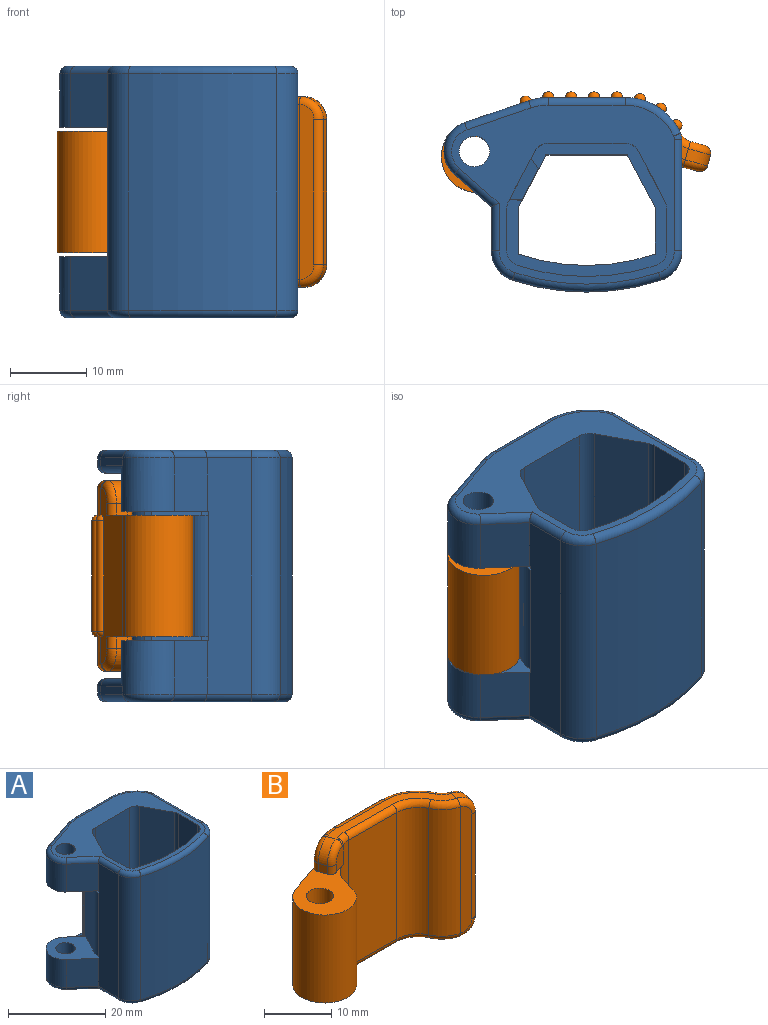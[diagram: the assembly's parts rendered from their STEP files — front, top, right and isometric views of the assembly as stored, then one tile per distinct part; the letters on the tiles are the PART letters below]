
ASSEMBLY  parts=2 mates=1
PART A: 107 faces, bbox 32x28.8x33 mm
  f0: plane 11.92x11.48mm, normal (0,0,1), area 71.6mm2, adj f7,f8,f9,f19,f23,f39,f40,f41
  f1: plane 21x17.5mm, normal (0,0,1), area 91.8mm2, adj f2,f3,f4,f5,f6,f20,f29,f30
  f2: plane 6.08x3mm, normal (1,0,0), area 18.2mm2, adj f1,f3,f20,f22
  f3: plane 6.93x3.65mm, normal (0.88,-0.47,0), area 23.5mm2, adj f1,f2,f4,f22
  f4: plane 10.69x3mm, normal (0,-1,0), area 32.1mm2, adj f1,f3,f5,f22
  f5: plane 6.93x3.65mm, normal (-0.88,-0.47,0), area 23.5mm2, adj f1,f4,f6,f22
  f6: plane 6.08x3mm, normal (-1,0,0), area 18.2mm2, adj f1,f5,f20,f22
  f7: cylinder r=4mm len=7.01mm, axis (0,0,-1), area 80.7mm2, adj f0,f8,f18,f21,f23,f76,f96
  f8: plane 7x4.87mm, normal (-0.66,-0.75,0), area 45.2mm2, adj f0,f7,f9,f78
  f9: plane 31x5.8mm, normal (-1,0,0), area 176.3mm2, adj f0,f8,f10,f43,f46,f52,f62,f77
  f10: cylinder r=4mm len=31mm, axis (0,0,-1), area 155.6mm2, adj f9,f11,f75,f87
  f11: cylinder r=31.35mm len=31mm, axis (0,0,-1), area 614.3mm2, adj f10,f12,f73,f85
  f12: cylinder r=4mm len=31mm, axis (0,0,-1), area 155.6mm2, adj f11,f13,f71,f83
  f13: plane 31x14.64mm, normal (1,0,0), area 191.5mm2, adj f12,f14,f24,f53,f69,f81,f91,f97
  f14: cylinder r=2mm len=1mm, axis (0,0,-1), area 0.9mm2, adj f13,f15,f67,f92
  f15: cylinder r=8mm len=7.28mm, axis (0,0,-1), area 9.1mm2, adj f14,f16,f68,f93
  f16: plane 10.09x1mm, normal (0,1,0), area 10.1mm2, adj f15,f17,f70,f94
  f17: cylinder r=8mm len=2.58mm, axis (0,0,-1), area 2.6mm2, adj f16,f18,f72,f95
  f18: plane 8.4x2.86mm, normal (-0.32,0.95,0), area 8.9mm2, adj f7,f17,f74,f96
  f19: cylinder r=2mm len=8mm, axis (0,0,-1), area 100.5mm2, adj f0,f22
  f20: cylinder r=27.85mm len=18mm, axis (0,0,-1), area 55mm2, adj f1,f2,f6,f22
  f21: plane 24.7x10.67mm, normal (0,0,1), area 81.7mm2, adj f7,f23,f25,f26,f27,f28,f41,f91
  f22: plane 29.23x23.5mm, normal (0,0,-1), area 314.2mm2, adj f2,f3,f4,f5,f6,f19,f20,f67
  f23: plane 5x3.15mm, normal (0.66,0.75,0), area 20.9mm2, adj f0,f7,f21,f41
  f24: cylinder r=4mm len=29mm, axis (0,0,-1), area 54.7mm2, adj f13,f25,f91,f97
  f25: plane 27.36x6.6mm, normal (0.88,0.47,0), area 200.1mm2, adj f21,f24,f26,f63,f91,f97
  f26: cylinder r=4mm len=27mm, axis (0,0,-1), area 117.2mm2, adj f21,f25,f27,f63
  f27: plane 27x10.09mm, normal (0,1,0), area 272.4mm2, adj f21,f26,f28,f63
  f28: cylinder r=4mm len=27mm, axis (0,0,-1), area 117.2mm2, adj f21,f27,f41,f42,f63,f66
  f29: cylinder r=2mm len=30mm, axis (0,0,-1), area 65.1mm2, adj f1,f30,f40,f42,f60,f64
  f30: plane 30x10.09mm, normal (0,-1,0), area 302.6mm2, adj f1,f29,f31,f64
  f31: cylinder r=2mm len=30mm, axis (0,0,-1), area 65.1mm2, adj f1,f30,f32,f64
  f32: plane 30x6.55mm, normal (-0.88,-0.47,0), area 222.2mm2, adj f1,f31,f33,f64
  f33: cylinder r=2mm len=30mm, axis (0,0,-1), area 29.1mm2, adj f1,f32,f34,f64
  f34: plane 30x5.59mm, normal (-1,0,0), area 167.8mm2, adj f1,f33,f35,f64
  f35: cylinder r=2mm len=30mm, axis (0,0,-1), area 75.3mm2, adj f1,f34,f36,f64
  f36: cylinder r=29.35mm len=30mm, axis (0,0,-1), area 556.5mm2, adj f1,f35,f37,f64
  f37: cylinder r=2mm len=30mm, axis (0,0,-1), area 75.3mm2, adj f1,f36,f38,f64
  f38: plane 30x5.59mm, normal (1,0,0), area 167.8mm2, adj f1,f37,f39,f43,f59,f64
  f39: cylinder r=2mm len=5mm, axis (0,0,-1), area 4.9mm2, adj f0,f1,f38,f40
  f40: plane 6.55x5mm, normal (0.88,-0.47,0), area 37mm2, adj f0,f1,f29,f39
  f41: plane 5x0.69mm, normal (-0.88,0.47,0), area 3.9mm2, adj f0,f21,f23,f28
  f42: plane 17x1.77mm, normal (-0.47,-0.88,0), area 34mm2, adj f0,f28,f29,f52
  f43: plane 17x2mm, normal (0,1,0), area 18mm2, adj f0,f9,f38,f47,f50,f51,f52
  f44: plane 16x1.33mm, normal (0.47,0.88,0), area 24mm2, adj f45,f50,f51,f103
  f45: plane 16x5.85mm, normal (-0.88,0.47,0), area 105.7mm2, adj f44,f46,f50,f51
  f46: cylinder r=4mm len=16mm, axis (0,0,-1), area 31.1mm2, adj f9,f45,f50,f51
  f47: cylinder r=3mm len=16mm, axis (0,0,-1), area 23.3mm2, adj f43,f48,f50,f51
  f48: plane 16x0.44mm, normal (-0.47,-0.88,0), area 8mm2, adj f47,f50,f51,f106
  f49: plane 14x4.08mm, normal (0.88,-0.47,0), area 64.5mm2, adj f103,f104,f105,f106
  f50: plane 7.71x4.87mm, normal (0,0,1), area 11.6mm2, adj f43,f44,f45,f46,f47,f48,f104
  f51: plane 7.71x4.87mm, normal (0,0,-1), area 11.6mm2, adj f43,f44,f45,f46,f47,f48,f105
  f52: plane 11.92x11.48mm, normal (0,0,-1), area 71.6mm2, adj f9,f42,f43,f58,f59,f60,f61,f62
  f53: cylinder r=2mm len=1mm, axis (0,0,1), area 0.9mm2, adj f13,f54,f79,f98
  f54: cylinder r=8mm len=7.28mm, axis (0,0,1), area 9.1mm2, adj f53,f55,f80,f99
  f55: plane 10.09x1mm, normal (0,1,0), area 10.1mm2, adj f54,f56,f82,f100
  f56: cylinder r=8mm len=2.58mm, axis (0,0,1), area 2.6mm2, adj f55,f57,f84,f101
  f57: plane 8.4x2.86mm, normal (-0.32,0.95,0), area 8.9mm2, adj f56,f58,f86,f102
  f58: cylinder r=4mm len=7.01mm, axis (0,0,1), area 80.7mm2, adj f52,f57,f62,f63,f65,f88,f102
  f59: cylinder r=2mm len=8mm, axis (0,0,1), area 7.8mm2, adj f38,f52,f60,f64
  f60: plane 8x6.55mm, normal (0.88,-0.47,0), area 59.3mm2, adj f29,f52,f59,f64
  f61: cylinder r=2mm len=8mm, axis (0,0,1), area 100.5mm2, adj f52,f64
  f62: plane 7x4.87mm, normal (-0.66,-0.75,0), area 45.2mm2, adj f9,f52,f58,f90
  f63: plane 24.7x10.67mm, normal (0,0,-1), area 81.7mm2, adj f25,f26,f27,f28,f58,f65,f66,f97
  f64: plane 29.23x23.5mm, normal (0,0,1), area 222.4mm2, adj f29,f30,f31,f32,f33,f34,f35,f36
  f65: plane 5x3.15mm, normal (0.66,0.75,0), area 20.9mm2, adj f52,f58,f63,f66
  f66: plane 5x0.69mm, normal (-0.88,0.47,0), area 3.9mm2, adj f28,f52,f63,f65
  f67: torus R=1mm, axis (0,0,1), area 1.1mm2, adj f14,f22,f68,f69
  f68: torus R=7mm, axis (0,0,1), area 13.7mm2, adj f15,f22,f67,f70
  f69: cylinder r=1mm len=14.64mm, axis (0,1,0), area 23mm2, adj f13,f22,f67,f71
  f70: cylinder r=1mm len=10.09mm, axis (-1,0,0), area 15.8mm2, adj f16,f22,f68,f72
  f71: torus R=3mm, axis (0,0,1), area 7.2mm2, adj f12,f22,f69,f73
  f72: torus R=7mm, axis (0,0,1), area 3.9mm2, adj f17,f22,f70,f74
  f73: torus R=30.35mm, axis (0,0,1), area 30.8mm2, adj f11,f22,f71,f75
  f74: cylinder r=1mm len=8.72mm, axis (-0.95,-0.32,0), area 13.9mm2, adj f18,f22,f72,f76
  f75: torus R=3mm, axis (0,0,1), area 7.2mm2, adj f10,f22,f73,f77
  f76: torus R=3mm, axis (0,0,1), area 12mm2, adj f7,f22,f74,f78
  f77: cylinder r=1mm len=6.26mm, axis (0,-1,0), area 9.5mm2, adj f9,f22,f75,f78
  f78: cylinder r=1mm len=5.87mm, axis (0.75,-0.66,0), area 10.5mm2, adj f8,f22,f76,f77
  f79: torus R=1mm, axis (0,0,-1), area 1.1mm2, adj f53,f64,f80,f81
  f80: torus R=7mm, axis (0,0,-1), area 13.7mm2, adj f54,f64,f79,f82
  f81: cylinder r=1mm len=14.64mm, axis (0,-1,0), area 23mm2, adj f13,f64,f79,f83
  f82: cylinder r=1mm len=10.09mm, axis (-1,0,0), area 15.8mm2, adj f55,f64,f80,f84
  f83: torus R=3mm, axis (0,0,-1), area 7.2mm2, adj f12,f64,f81,f85
  f84: torus R=7mm, axis (0,0,-1), area 3.9mm2, adj f56,f64,f82,f86
  f85: torus R=30.35mm, axis (0,0,-1), area 30.8mm2, adj f11,f64,f83,f87
  f86: cylinder r=1mm len=8.72mm, axis (-0.95,-0.32,0), area 13.9mm2, adj f57,f64,f84,f88
  f87: torus R=3mm, axis (0,0,-1), area 7.2mm2, adj f10,f64,f85,f89
  f88: torus R=3mm, axis (0,0,-1), area 12mm2, adj f58,f64,f86,f90
  f89: cylinder r=1mm len=6.26mm, axis (0,1,0), area 9.5mm2, adj f9,f64,f87,f90
  f90: cylinder r=1mm len=5.87mm, axis (0.75,-0.66,0), area 10.5mm2, adj f62,f64,f88,f89
  f91: cylinder r=1mm len=9.05mm, axis (0,-1,0), area 11.9mm2, adj f13,f21,f24,f25,f92
  f92: torus R=1mm, axis (0,0,1), area 1.1mm2, adj f14,f21,f91,f93
  f93: torus R=7mm, axis (0,0,1), area 13.7mm2, adj f15,f21,f92,f94
  f94: cylinder r=1mm len=10.09mm, axis (1,0,0), area 15.8mm2, adj f16,f21,f93,f95
  f95: torus R=7mm, axis (0,0,1), area 3.9mm2, adj f17,f21,f94,f96
  f96: cylinder r=1mm len=8.72mm, axis (0.95,0.32,0), area 11.9mm2, adj f7,f18,f21,f95
  f97: cylinder r=1mm len=9.05mm, axis (0,1,0), area 11.9mm2, adj f13,f24,f25,f63,f98
  f98: torus R=1mm, axis (0,0,-1), area 1.1mm2, adj f53,f63,f97,f99
  f99: torus R=7mm, axis (0,0,-1), area 13.7mm2, adj f54,f63,f98,f100
  f100: cylinder r=1mm len=10.09mm, axis (1,0,0), area 15.8mm2, adj f55,f63,f99,f101
  f101: torus R=7mm, axis (0,0,-1), area 3.9mm2, adj f56,f63,f100,f102
  f102: cylinder r=1mm len=8.72mm, axis (0.95,0.32,0), area 11.9mm2, adj f57,f58,f63,f101
  f103: plane 16x1.82mm, normal (0.81,0.58,0), area 33.5mm2, adj f44,f49,f104,f105
  f104: plane 5.89x4.39mm, normal (0.4,-0.21,0.89), area 12.5mm2, adj f49,f50,f103,f106
  f105: plane 5.89x4.39mm, normal (0.4,-0.21,-0.89), area 12.5mm2, adj f49,f51,f103,f106
  f106: plane 16x2.24mm, normal (-0.02,-1,0), area 33.5mm2, adj f48,f49,f104,f105
PART B: 87 faces, bbox 35.6x13.3x25.6 mm
  f0: cylinder r=2mm len=23mm, axis (0,0,-1), area 40.1mm2, adj f1,f13,f60,f64
  f1: cylinder r=8mm len=23mm, axis (0,0,-1), area 141.4mm2, adj f0,f2,f22,f23,f24,f59,f65,f71
  f2: plane 23x10.09mm, normal (0,1,0), area 149.7mm2, adj f1,f3,f25,f26,f27,f28,f58,f66
  f3: cylinder r=8mm len=23mm, axis (0,0,-1), area 43.5mm2, adj f2,f4,f17,f28,f57,f67,f77,f78
  f4: plane 23.07x8.46mm, normal (-0.32,0.95,0), area 138.9mm2, adj f3,f15,f16,f17,f18,f54,f55,f56
  f5: plane 1.5x1.42mm, normal (-0.95,-0.32,0), area 2.3mm2, adj f15,f36,f53,f70
  f6: plane 3.5x2.25mm, normal (0.32,-0.95,0), area 7.4mm2, adj f7,f15,f51,f52,f53
  f7: cylinder r=4.5mm len=23mm, axis (0,0,-1), area 104.7mm2, adj f6,f8,f15,f16,f21,f31,f40,f50
  f8: plane 23x10.09mm, normal (0,-1,0), area 232mm2, adj f7,f9,f41,f49
  f9: cylinder r=4.5mm len=23mm, axis (0,0,-1), area 118.2mm2, adj f8,f10,f42,f48
  f10: cylinder r=5.5mm len=23mm, axis (0,0,-1), area 110.4mm2, adj f9,f11,f43,f47
  f11: plane 23x1.93mm, normal (-0.27,-0.96,0), area 44.3mm2, adj f10,f44,f45,f46
  f12: plane 19x1.45mm, normal (0.96,-0.27,0), area 28.5mm2, adj f33,f35,f45,f62
  f13: plane 23x1.93mm, normal (0.27,0.96,0), area 44.3mm2, adj f0,f61,f62,f63
  f14: plane 21x7.18mm, normal (0,0,-1), area 34.4mm2, adj f35,f36,f47,f48,f49,f50,f51,f64
  f15: plane 12.59x11.27mm, normal (0,0,-1), area 67.8mm2, adj f4,f5,f6,f7,f18,f19,f20,f21
  f16: plane 12.59x11.27mm, normal (0,0,1), area 67.8mm2, adj f4,f7,f18,f19,f20,f21,f29,f30
  f17: cylinder r=0.75mm len=14.5mm, axis (0,0,-1), area 34.3mm2, adj f3,f4,f78,f86
  f18: cylinder r=4mm len=16mm, axis (0,0,-1), area 14.9mm2, adj f4,f15,f16,f19
  f19: cylinder r=4.75mm len=16mm, axis (0,0,-1), area 238.8mm2, adj f15,f16,f18,f20
  f20: cylinder r=4mm len=16mm, axis (0,0,-1), area 47.9mm2, adj f15,f16,f19,f21
  f21: plane 16x2.54mm, normal (0.97,-0.26,0), area 42mm2, adj f7,f15,f16,f20
  f22: cylinder r=0.75mm len=14.5mm, axis (0,0,-1), area 35.2mm2, adj f1,f73,f81
  f23: cylinder r=0.75mm len=14.5mm, axis (0,0,-1), area 35.2mm2, adj f1,f72,f80
  f24: cylinder r=0.75mm len=14.5mm, axis (0,0,-1), area 35.2mm2, adj f1,f71,f79
  f25: cylinder r=0.75mm len=14.5mm, axis (0,0,-1), area 34.2mm2, adj f2,f74,f82
  f26: cylinder r=0.75mm len=14.5mm, axis (0,0,-1), area 34.2mm2, adj f2,f75,f83
  f27: cylinder r=0.75mm len=14.5mm, axis (0,0,-1), area 34.2mm2, adj f2,f76,f84
  f28: cylinder r=0.75mm len=14.5mm, axis (0,0,-1), area 34.7mm2, adj f2,f3,f77,f85
  f29: cylinder r=2mm len=16mm, axis (0,0,-1), area 201.1mm2, adj f15,f16
  f30: plane 1.5x1.42mm, normal (-0.95,-0.32,0), area 2.3mm2, adj f16,f34,f37,f54
  f31: plane 3.5x2.25mm, normal (0.32,-0.95,0), area 7.4mm2, adj f7,f16,f37,f38,f39
  f32: plane 21x7.18mm, normal (0,0,1), area 34.4mm2, adj f33,f34,f39,f40,f41,f42,f43,f56
  f33: cylinder r=3mm len=3.29mm, axis (-0.27,-0.96,0), area 7.1mm2, adj f12,f32,f44,f61
  f34: cylinder r=3mm len=3.32mm, axis (-0.32,0.95,0), area 7.1mm2, adj f30,f32,f38,f55
  f35: cylinder r=3mm len=3.29mm, axis (0.27,0.96,0), area 7.1mm2, adj f12,f14,f46,f63
  f36: cylinder r=3mm len=3.32mm, axis (0.32,-0.95,0), area 7.1mm2, adj f5,f14,f52,f69
  f37: cylinder r=1mm len=1.5mm, axis (0,0,-1), area 2.4mm2, adj f16,f30,f31,f38
  f38: torus R=2mm, axis (-0.32,0.95,0), area 6.5mm2, adj f31,f34,f37,f39
  f39: cylinder r=1mm len=1.07mm, axis (-0.95,-0.32,0), area 0.6mm2, adj f31,f32,f38,f40
  f40: torus R=5.5mm, axis (0,0,1), area 2.5mm2, adj f7,f32,f39,f41
  f41: cylinder r=1mm len=10.09mm, axis (-1,0,0), area 15.8mm2, adj f8,f32,f40,f42
  f42: torus R=5.5mm, axis (0,0,1), area 8.7mm2, adj f9,f32,f41,f43
  f43: torus R=4.5mm, axis (0,0,1), area 7mm2, adj f10,f32,f42,f44
  f44: torus R=2mm, axis (0.27,0.96,0), area 6.5mm2, adj f11,f33,f43,f45
  f45: cylinder r=1mm len=19mm, axis (0,0,-1), area 29.8mm2, adj f11,f12,f44,f46
  f46: torus R=2mm, axis (0.27,0.96,0), area 6.5mm2, adj f11,f35,f45,f47
  f47: torus R=4.5mm, axis (0,0,1), area 7mm2, adj f10,f14,f46,f48
  f48: torus R=5.5mm, axis (0,0,1), area 8.7mm2, adj f9,f14,f47,f49
  f49: cylinder r=1mm len=10.09mm, axis (1,0,0), area 15.8mm2, adj f8,f14,f48,f50
  f50: torus R=5.5mm, axis (0,0,1), area 2.5mm2, adj f7,f14,f49,f51
  f51: cylinder r=1mm len=1.07mm, axis (0.95,0.32,0), area 0.6mm2, adj f6,f14,f50,f52
  f52: torus R=2mm, axis (-0.32,0.95,0), area 6.5mm2, adj f6,f36,f51,f53
  f53: cylinder r=1mm len=1.5mm, axis (0,0,-1), area 2.4mm2, adj f5,f6,f15,f52
  f54: cylinder r=1mm len=1.5mm, axis (0,0,-1), area 2.4mm2, adj f4,f16,f30,f55
  f55: torus R=2mm, axis (0.32,-0.95,0), area 6.5mm2, adj f4,f34,f54,f56
  f56: cylinder r=1mm len=1.07mm, axis (0.95,0.32,0), area 0.6mm2, adj f4,f32,f55,f57
  f57: torus R=7mm, axis (0,0,1), area 3.9mm2, adj f3,f32,f56,f58
  f58: cylinder r=1mm len=10.09mm, axis (1,0,0), area 15.8mm2, adj f2,f32,f57,f59
  f59: torus R=7mm, axis (0,0,1), area 13.7mm2, adj f1,f32,f58,f60
  f60: torus R=3mm, axis (0,0,1), area 3.2mm2, adj f0,f32,f59,f61
  f61: torus R=2mm, axis (0.27,0.96,0), area 6.5mm2, adj f13,f33,f60,f62
  f62: cylinder r=1mm len=19mm, axis (0,0,1), area 29.8mm2, adj f12,f13,f61,f63
  f63: torus R=2mm, axis (0.27,0.96,0), area 6.5mm2, adj f13,f35,f62,f64
  f64: torus R=3mm, axis (0,0,1), area 3.2mm2, adj f0,f14,f63,f65
  f65: torus R=7mm, axis (0,0,1), area 13.7mm2, adj f1,f14,f64,f66
  f66: cylinder r=1mm len=10.09mm, axis (-1,0,0), area 15.8mm2, adj f2,f14,f65,f67
  f67: torus R=7mm, axis (0,0,1), area 3.9mm2, adj f3,f14,f66,f68
  f68: cylinder r=1mm len=1.07mm, axis (-0.95,-0.32,0), area 0.6mm2, adj f4,f14,f67,f69
  f69: torus R=2mm, axis (0.32,-0.95,0), area 6.5mm2, adj f4,f36,f68,f70
  f70: cylinder r=1mm len=1.5mm, axis (0,0,-1), area 2.4mm2, adj f4,f5,f15,f69
  f71: sphere r=0.75mm, area 1.8mm2, adj f1,f24
  f72: sphere r=0.75mm, area 1.7mm2, adj f1,f23
  f73: sphere r=0.75mm, area 1.6mm2, adj f1,f22
  f74: sphere r=0.75mm, area 1.8mm2, adj f2,f25
  f75: sphere r=0.75mm, area 1.8mm2, adj f2,f26
  f76: sphere r=0.75mm, area 1.8mm2, adj f2,f27
  f77: sphere r=0.75mm, area 1.8mm2, adj f2,f3,f28
  f78: sphere r=0.75mm, area 1.8mm2, adj f3,f4,f17
  f79: sphere r=0.75mm, area 1.8mm2, adj f1,f24
  f80: sphere r=0.75mm, area 1.8mm2, adj f1,f23
  f81: sphere r=0.75mm, area 1.8mm2, adj f1,f22
  f82: sphere r=0.75mm, area 1.8mm2, adj f2,f25
  f83: sphere r=0.75mm, area 1.8mm2, adj f2,f26
  f84: sphere r=0.75mm, area 1.8mm2, adj f2,f27
  f85: sphere r=0.75mm, area 1.8mm2, adj f2,f3,f28
  f86: sphere r=0.75mm, area 1.8mm2, adj f3,f4,f17
PLACE A t=(-39.85,27.79,-19.96)mm fixed
PLACE B rot(axis=(0,0,-1),0deg) t=(-39.85,27.79,-19.96)mm
MATE revolute A.f7 <-> B.f18  axis (0,0,-1) through (-54.58,14.86,5.04)mm
